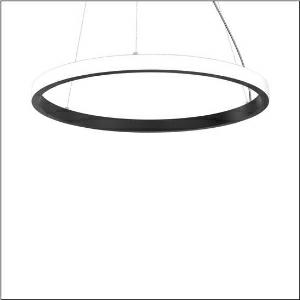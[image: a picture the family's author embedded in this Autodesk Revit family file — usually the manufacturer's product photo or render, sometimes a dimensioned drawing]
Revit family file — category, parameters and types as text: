
# Revit family: silica_21_ring-o_5pjbo4d3104a
name_source: partatom
category: Lighting Fixtures
units: mm (PartAtom-declared; Revit-internal decimal feet)

## family parameters
Cut with Voids When Loaded = No
Host = Face
Light Source = No
Part Type = Normal
Room Calculation Point = No
Round Connector Dimension = Use Diameter
Shared = No

## types (1)
- Silica 21 Ring-O (1 x LED, 9260 lm, 140 W, 4000K)
    Apparent Load = 140 VA
    CIE Flux Codes = 2 16 49 50 100
    Color Rendering = 80
    Color Temperature = 4000K
    Default Elevation = 1800 mm
    Description = Silica 21 Ring-O, suspended luminaire, of PMMA, frosted, light emission: outer ring side luminous distribution, primary light characteristic: symmetric, installation type: suspended mounting, LED, rated luminous flux: 9.260lm, luminous efficacy: 66lm/W, light colour: 840, colour temperature: 4000K, control gear: DALI 2, with terminal, 5-pole, mains connection: 230V, AC/DC, 0/50..60Hz, rated input power: 140W, housing, of extruded aluminium section, jet black (RAL 9005), diameter: 1.480mm, ceiling canopy, jet black (RAL 9005), protection rating (lamp compartment): IP40, insulation class (complete): insulation class I (protective earthing), certification: CE, impact resistance: IK02, permissible operating ambient temperature: 0..+35°C, packaging unit: 1 piece
    Height = 48 mm  [stored 0.15748 ft]
    Lamp = 1 x LED
    Lamp Light Flux = 9260 lm
    Lamp Power = 140 W
    Lamp count = 1
    Length = 1480 mm
    Luminous efficacy = 66 lm/W
    Manufacturer = Siteco
    ModVariant = No
    Model = 5PJBO4D3104A
    Mounting Place = Ceiling
    Mounting Type = Pendant
    Number of Poles = 1
    OnlyDefault = Yes
    Power Factor = 1
    Product Name = Silica 21 Ring-O
    Product group = suspended luminaire
    ProductGroupID = 904
    Protection Class = Protection class I
    Protection Degree = IP 40
    RLX_Detail_Level = 1
    RLX_Emergency_Light_Flux = 0 lm
    RLX_Emergency_Type = 0
    RLX_Emergency_Type_DB = No
    RlxData = <blob elided: 20549 chars, md5=d6e202b3>
    Socket = socket
    Standby Power = 0 W
    System Light Flux = 9260 lm
    System Power = 140 W
    Type Comments = Product without accessories
    Type Image = l_1258389.jpg
    URL = http://relux.com
    VarID = ---
    Voltage = 0 V
    Weight = 0.00 kg
    Width = 0 mm  [stored 0 ft]

note: [stored X ft] marks values corroborated as IEEE doubles in the binary element streams (Revit-internal decimal feet)

## geometry (parser evidence)
native form markers: Blend x4, Sweep x12
no freeform markers — native parametric forms only
